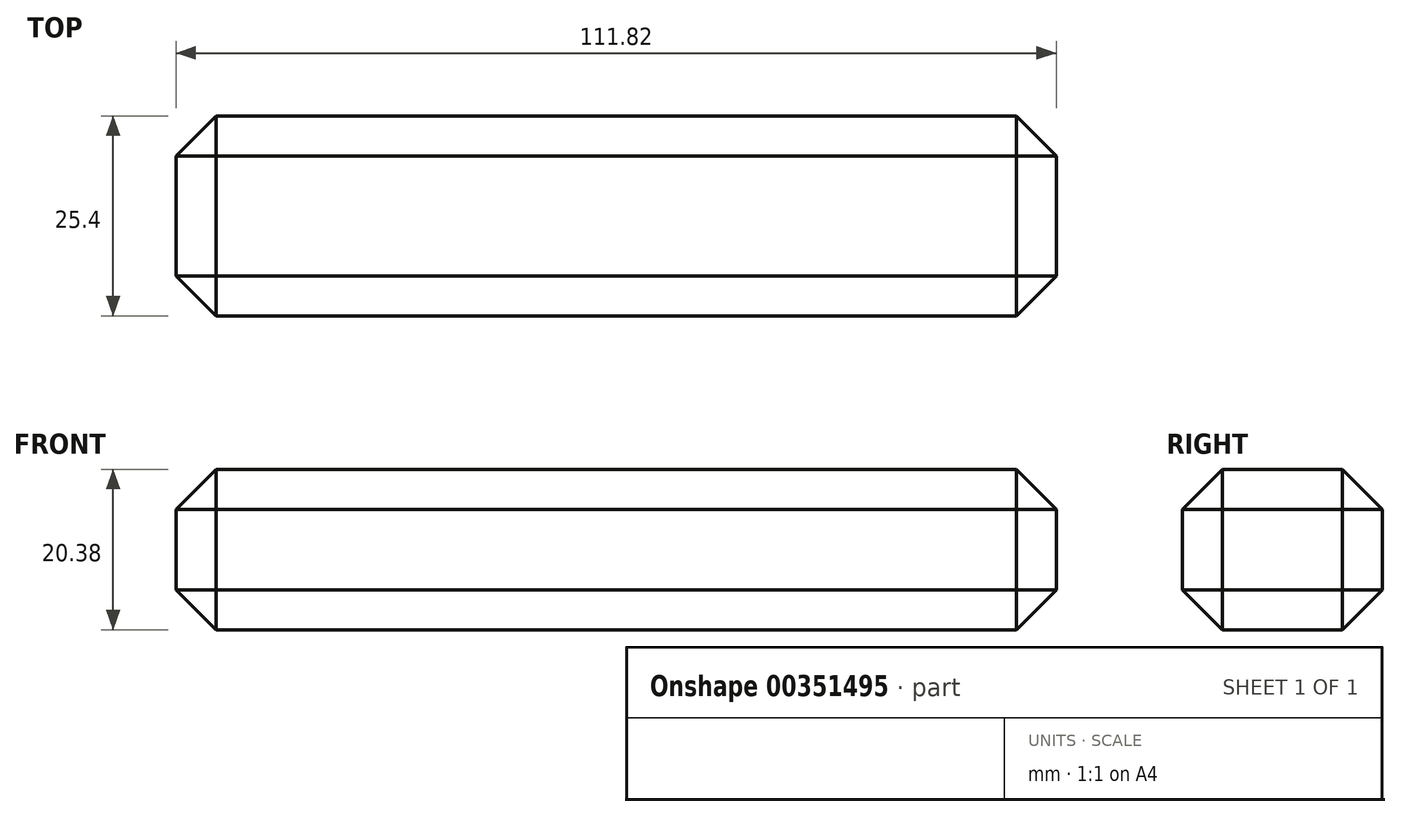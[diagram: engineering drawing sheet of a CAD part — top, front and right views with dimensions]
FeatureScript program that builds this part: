
annotation { "Feature Type Name" : "Feature", "Feature Type Description" : "" }
export const myFeature = defineFeature(function(context is Context, id is Id, definition is map)
    precondition{}
    {
        {
            var Q0;
            Q0=qCreatedBy(makeId("Front.planeOp"),FACE);
            var sketch = newSketch(context, id + "F0", { "sketchPlane" : qUnion([Q0])});
            skLineSegment(sketch, "E0", {"start": v(-55.91, 16.06) * mm, "end": v(55.91, 16.06) * mm});
            skLineSegment(sketch, "E1", {"start": v(55.91, 16.06) * mm, "end": v(55.91, -4.32) * mm});
            skLineSegment(sketch, "E2", {"start": v(55.91, -4.32) * mm, "end": v(-55.91, -4.32) * mm});
            skLineSegment(sketch, "E3", {"start": v(-55.91, -4.32) * mm, "end": v(-55.91, 16.06) * mm});
            skSolve(sketch);
        }
        {
            var Q0;
            Q0=makeQuery(id+"F0.imprint","IMPRINT",FACE,{"disambiguationData":[TD([[makeQuery(id+"F0.imprint","IMPRINT",EDGE,{"derivedFrom":sQuery(id+"F0.wireOp",EDGE,"E0")}),-1.0]])]});
            extrude(context, id + "F1", {"entities" : qUnion([Q0]), "depth" : 25.4 * mm});
        }
        {
            var Q0;
            Q0=makeQuery(id+"F1.opExtrude","CAP_EDGE",EDGE,{"disambiguationData":[OSD([sQuery(id+"F0.wireOp",EDGE,"E2")])],"isStart":false});
            var Q1;
            Q1=makeQuery(id+"F1.opExtrude","CAP_FACE",FACE,{"disambiguationData":[OSD([sQuery(id+"F0.wireOp",EDGE,"E0"),sQuery(id+"F0.wireOp",EDGE,"E1"),sQuery(id+"F0.wireOp",EDGE,"E2"),sQuery(id+"F0.wireOp",EDGE,"E3")])],"isStart":false});
            var Q2;
            Q2=makeQuery(id+"F1.opExtrude","SWEPT_FACE",FACE,{"disambiguationData":[OSD([sQuery(id+"F0.wireOp",EDGE,"E3")])]});
            var Q3;
            Q3=makeQuery(id+"F1.opExtrude","CAP_FACE",FACE,{"disambiguationData":[OSD([sQuery(id+"F0.wireOp",EDGE,"E0"),sQuery(id+"F0.wireOp",EDGE,"E1"),sQuery(id+"F0.wireOp",EDGE,"E2"),sQuery(id+"F0.wireOp",EDGE,"E3")])],"isStart":true});
            var Q4;
            Q4=makeQuery(id+"F1.opExtrude","SWEPT_FACE",FACE,{"disambiguationData":[OSD([sQuery(id+"F0.wireOp",EDGE,"E0")])]});
            var Q5;
            Q5=makeQuery(id+"F1.opExtrude","SWEPT_FACE",FACE,{"disambiguationData":[OSD([sQuery(id+"F0.wireOp",EDGE,"E1")])]});
            chamfer(context, id + "F2", {"entities" : qUnion([Q0, Q1, Q2, Q3, Q4, Q5]), "width" : 5.08 * mm, "tangentPropagation" : true});
        }
    });
